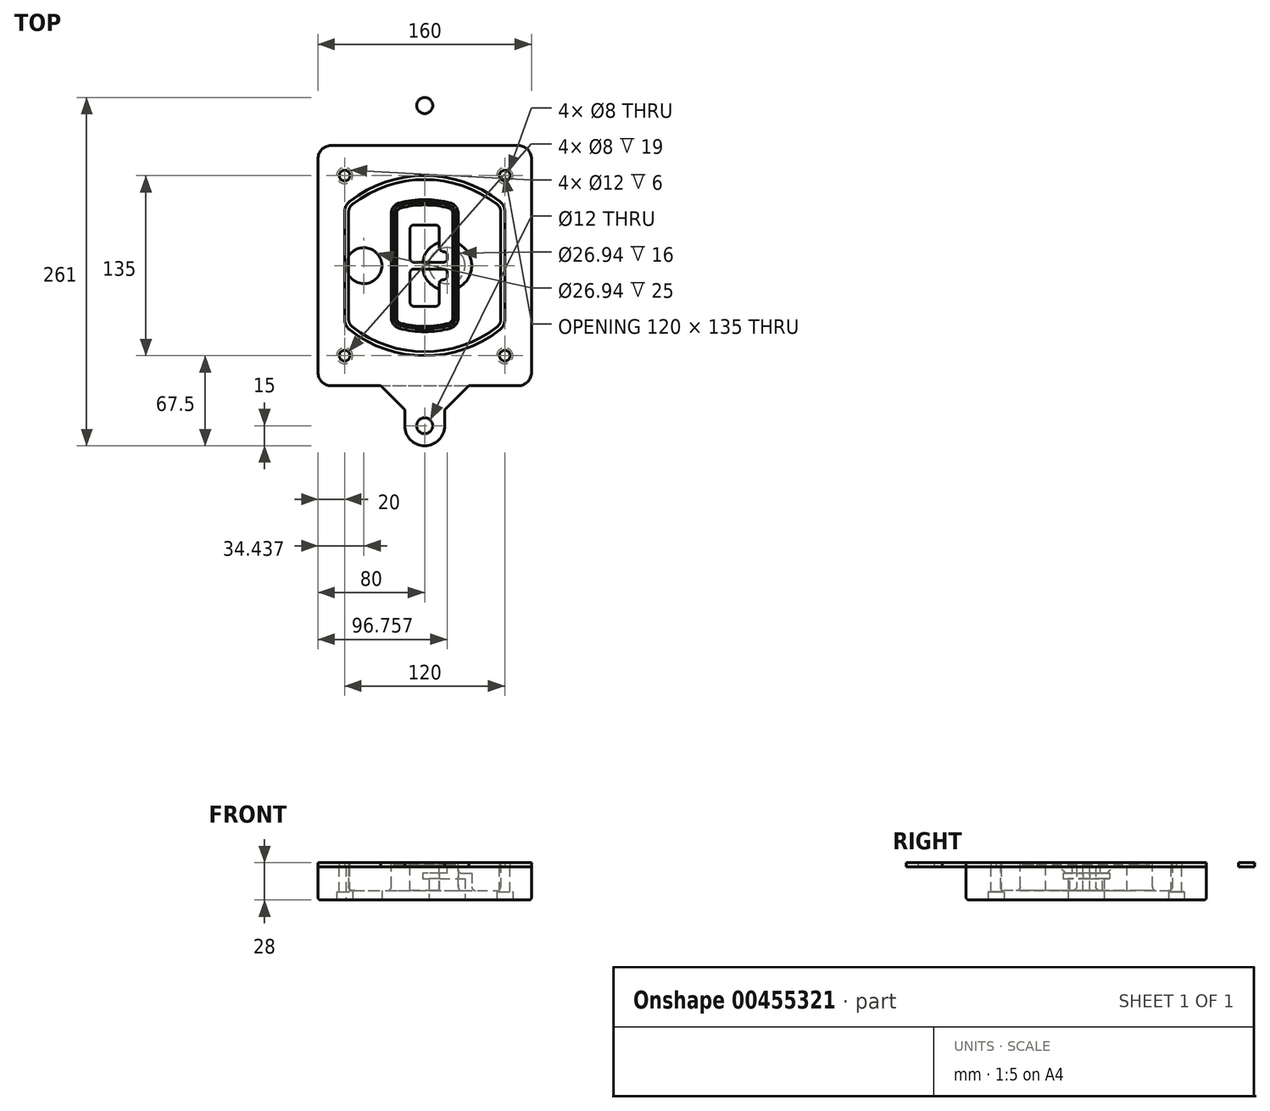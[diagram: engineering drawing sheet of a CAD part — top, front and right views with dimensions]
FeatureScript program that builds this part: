
annotation { "Feature Type Name" : "Feature", "Feature Type Description" : "" }
export const myFeature = defineFeature(function(context is Context, id is Id, definition is map)
    precondition{}
    {
        {
            var Q0;
            Q0=qCreatedBy(makeId("Top.planeOp"),FACE);
            var sketch = newSketch(context, id + "F0", { "sketchPlane" : qUnion([Q0])});
            skPoint(sketch, "E0.rect.middle", {"position": v(0, 0) * mm});
            skLineSegment(sketch, "E1.bottom", {"start": v(-70, -90) * mm, "end": v(70, -90) * mm});
            skLineSegment(sketch, "E1.top", {"start": v(-70, 90) * mm, "end": v(70, 90) * mm});
            skLineSegment(sketch, "E1.left", {"start": v(-80, -80) * mm, "end": v(-80, 80) * mm});
            skLineSegment(sketch, "E1.right", {"start": v(80, -80) * mm, "end": v(80, 80) * mm});
            skLineSegment(sketch, "E2", {"start": v(-80, 90) * mm, "end": v(80, -90) * mm, "construction": true});
            skLineSegment(sketch, "E3", {"start": v(80, 90) * mm, "end": v(-80, -90) * mm, "construction": true});
            skCircle(sketch, "E4", {"center": v(-60, 67.5) * mm, "radius": 4 * mm});
            skCircle(sketch, "E5", {"center": v(60, 67.5) * mm, "radius": 4 * mm});
            skCircle(sketch, "E6", {"center": v(60, -67.5) * mm, "radius": 4 * mm});
            skCircle(sketch, "E7", {"center": v(-60, -67.5) * mm, "radius": 4 * mm});
            skLineSegment(sketch, "E8", {"start": v(-60, 67.5) * mm, "end": v(60, 67.5) * mm, "construction": true});
            skLineSegment(sketch, "E9", {"start": v(60, 67.5) * mm, "end": v(60, -67.5) * mm, "construction": true});
            skLineSegment(sketch, "E10", {"start": v(60, -67.5) * mm, "end": v(-60, -67.5) * mm, "construction": true});
            skLineSegment(sketch, "E11", {"start": v(-60, -67.5) * mm, "end": v(-60, 67.5) * mm, "construction": true});
            skLineSegment(sketch, "E12", {"start": v(-60, 40.3) * mm, "end": v(-60, -40.3) * mm});
            skLineSegment(sketch, "E13", {"start": v(60, 40.3) * mm, "end": v(60, -40.3) * mm});
            skArc(sketch, "E14", {"start": v(56.15, 48.18) * mm, "mid": v(0, 67.5) * mm, "end": v(-56.15, 48.18) * mm});
            skArc(sketch, "E15", {"start": v(-56.15, -48.18) * mm, "mid": v(0, -67.5) * mm, "end": v(56.15, -48.18) * mm});
            skLineSegment(sketch, "E16", {"start": v(-60, 0) * mm, "end": v(60, 0) * mm, "construction": true});
            skPoint(sketch, "E17.visualSharp", {"position": v(-60, -45) * mm});
            skArc(sketch, "E17.filletArc", {"start": v(-60, -40.3) * mm, "mid": v(-58.99, -44.68) * mm, "end": v(-56.15, -48.18) * mm});
            skPoint(sketch, "E18.visualSharp", {"position": v(-60, 45) * mm});
            skArc(sketch, "E18.filletArc", {"start": v(-56.15, 48.18) * mm, "mid": v(-58.99, 44.68) * mm, "end": v(-60, 40.3) * mm});
            skPoint(sketch, "E19.visualSharp", {"position": v(60, 45) * mm});
            skArc(sketch, "E19.filletArc", {"start": v(60, 40.3) * mm, "mid": v(58.99, 44.68) * mm, "end": v(56.15, 48.18) * mm});
            skPoint(sketch, "E20.visualSharp", {"position": v(60, -45) * mm});
            skArc(sketch, "E20.filletArc", {"start": v(56.15, -48.18) * mm, "mid": v(58.99, -44.68) * mm, "end": v(60, -40.3) * mm});
            skPoint(sketch, "E21.visualSharp", {"position": v(-80, 90) * mm});
            skArc(sketch, "E21.filletArc", {"start": v(-70, 90) * mm, "mid": v(-77.07, 87.07) * mm, "end": v(-80, 80) * mm});
            skPoint(sketch, "E22.visualSharp", {"position": v(80, 90) * mm});
            skArc(sketch, "E22.filletArc", {"start": v(80, 80) * mm, "mid": v(77.07, 87.07) * mm, "end": v(70, 90) * mm});
            skPoint(sketch, "E23.visualSharp", {"position": v(80, -90) * mm});
            skArc(sketch, "E23.filletArc", {"start": v(70, -90) * mm, "mid": v(77.07, -87.07) * mm, "end": v(80, -80) * mm});
            skPoint(sketch, "E24.visualSharp", {"position": v(-80, -90) * mm});
            skArc(sketch, "E24.filletArc", {"start": v(-80, -80) * mm, "mid": v(-77.07, -87.07) * mm, "end": v(-70, -90) * mm});
            skArc(sketch, "E25.0", {"start": v(57, 40.3) * mm, "mid": v(56.3, 43.36) * mm, "end": v(54.3, 45.81) * mm});
            skLineSegment(sketch, "E25.1", {"start": v(57, 40.3) * mm, "end": v(57, -40.3) * mm});
            skArc(sketch, "E25.2", {"start": v(54.3, -45.81) * mm, "mid": v(56.3, -43.36) * mm, "end": v(57, -40.3) * mm});
            skArc(sketch, "E25.3", {"start": v(-54.3, -45.81) * mm, "mid": v(0, -64.5) * mm, "end": v(54.3, -45.81) * mm});
            skArc(sketch, "E25.4", {"start": v(-57, -40.3) * mm, "mid": v(-56.3, -43.36) * mm, "end": v(-54.3, -45.81) * mm});
            skArc(sketch, "E25.5", {"start": v(54.3, 45.81) * mm, "mid": v(0, 64.5) * mm, "end": v(-54.3, 45.81) * mm});
            skLineSegment(sketch, "E25.6", {"start": v(-57, 40.3) * mm, "end": v(-57, -40.3) * mm});
            skArc(sketch, "E25.7", {"start": v(-54.3, 45.81) * mm, "mid": v(-56.3, 43.36) * mm, "end": v(-57, 40.3) * mm});
            skArc(sketch, "E26.0", {"start": v(-58.62, 51.33) * mm, "mid": v(-62.58, 46.43) * mm, "end": v(-64, 40.3) * mm});
            skArc(sketch, "E26.1", {"start": v(58.62, 51.33) * mm, "mid": v(0, 71.5) * mm, "end": v(-58.62, 51.33) * mm});
            skArc(sketch, "E26.2", {"start": v(64, 40.3) * mm, "mid": v(62.58, 46.43) * mm, "end": v(58.62, 51.33) * mm});
            skLineSegment(sketch, "E26.3", {"start": v(64, 40.3) * mm, "end": v(64, -40.3) * mm});
            skArc(sketch, "E26.4", {"start": v(58.62, -51.33) * mm, "mid": v(62.58, -46.43) * mm, "end": v(64, -40.3) * mm});
            skLineSegment(sketch, "E26.5", {"start": v(-64, 40.3) * mm, "end": v(-64, -40.3) * mm});
            skArc(sketch, "E26.6", {"start": v(-58.62, -51.33) * mm, "mid": v(0, -71.5) * mm, "end": v(58.62, -51.33) * mm});
            skArc(sketch, "E26.7", {"start": v(-64, -40.3) * mm, "mid": v(-62.58, -46.43) * mm, "end": v(-58.62, -51.33) * mm});
            skSolve(sketch);
        }
        {
            var Q0;
            Q0=makeQuery(id+"F0.imprint","IMPRINT",FACE,{"disambiguationData":[TD([[makeQuery(id+"F0.imprint","IMPRINT",EDGE,{"derivedFrom":sQuery(id+"F0.wireOp",EDGE,"E1.bottom")}),1.0]])]});
            var Q1;
            Q1=makeQuery(id+"F0.imprint","IMPRINT",FACE,{"disambiguationData":[TD([[makeQuery(id+"F0.imprint","IMPRINT",EDGE,{"derivedFrom":sQuery(id+"F0.wireOp",EDGE,"E12")}),1.0]])]});
            var Q2;
            Q2=makeQuery(id+"F0.imprint","IMPRINT",FACE,{"disambiguationData":[TD([[makeQuery(id+"F0.imprint","IMPRINT",EDGE,{"derivedFrom":sQuery(id+"F0.wireOp",EDGE,"E25.0")}),1.0]])]});
            var Q3;
            Q3=makeQuery(id+"F0.imprint","IMPRINT",FACE,{"disambiguationData":[TD([[makeQuery(id+"F0.imprint","IMPRINT",EDGE,{"derivedFrom":sQuery(id+"F0.wireOp",EDGE,"E12")}),-1.0]])]});
            extrude(context, id + "F1", {"entities" : qUnion([Q0, Q1, Q2, Q3]), "oppositeDirection" : true, "depth" : 25 * mm});
        }
        {
            var Q0;
            Q0=makeQuery(id+"F0.imprint","IMPRINT",FACE,{"disambiguationData":[TD([[makeQuery(id+"F0.imprint","IMPRINT",EDGE,{"derivedFrom":sQuery(id+"F0.wireOp",EDGE,"E12")}),1.0]])]});
            extrude(context, id + "F2", {"entities" : qUnion([Q0]), "operationType" : NewBodyOperationType.ADD, "depth" : 3 * mm});
        }
        {
            var Q0;
            Q0=makeQuery(id+"F0.imprint","IMPRINT",FACE,{"disambiguationData":[TD([[makeQuery(id+"F0.imprint","IMPRINT",EDGE,{"derivedFrom":sQuery(id+"F0.wireOp",EDGE,"E25.0")}),1.0]])]});
            extrude(context, id + "F3", {"entities" : qUnion([Q0]), "operationType" : NewBodyOperationType.REMOVE, "oppositeDirection" : true, "depth" : 18 * mm});
        }
        {
            var Q0;
            Q0=makeQuery(id+"F2.opExtrude","CAP_FACE",FACE,{"disambiguationData":[OSD([sQuery(id+"F0.wireOp",EDGE,"E12"),sQuery(id+"F0.wireOp",EDGE,"E13"),sQuery(id+"F0.wireOp",EDGE,"E14"),sQuery(id+"F0.wireOp",EDGE,"E15"),sQuery(id+"F0.wireOp",EDGE,"E17.filletArc"),sQuery(id+"F0.wireOp",EDGE,"E18.filletArc"),sQuery(id+"F0.wireOp",EDGE,"E19.filletArc"),sQuery(id+"F0.wireOp",EDGE,"E20.filletArc"),sQuery(id+"F0.wireOp",EDGE,"E25.0"),sQuery(id+"F0.wireOp",EDGE,"E25.1"),sQuery(id+"F0.wireOp",EDGE,"E25.2"),sQuery(id+"F0.wireOp",EDGE,"E25.3"),sQuery(id+"F0.wireOp",EDGE,"E25.4"),sQuery(id+"F0.wireOp",EDGE,"E25.5"),sQuery(id+"F0.wireOp",EDGE,"E25.6"),sQuery(id+"F0.wireOp",EDGE,"E25.7")])],"isStart":false});
            var sketch = newSketch(context, id + "F4", { "sketchPlane" : qUnion([Q0])});
            skArc(sketch, "E27.0", {"start": v(-19.08, -46.97) * mm, "mid": v(0, -49.5) * mm, "end": v(19.08, -46.97) * mm});
            skArc(sketch, "E28.0", {"start": v(19.08, 46.97) * mm, "mid": v(0, 49.5) * mm, "end": v(-19.08, 46.97) * mm});
            skLineSegment(sketch, "E29", {"start": v(-25, 39.25) * mm, "end": v(-25, -39.25) * mm});
            skLineSegment(sketch, "E30", {"start": v(25, 39.25) * mm, "end": v(25, -39.25) * mm});
            skLineSegment(sketch, "E31", {"start": v(-25, 45.1) * mm, "end": v(25, 45.1) * mm, "construction": true});
            skLineSegment(sketch, "E32", {"start": v(-25, -45.1) * mm, "end": v(25, -45.1) * mm, "construction": true});
            skPoint(sketch, "E33.visualSharp", {"position": v(-25, 45.1) * mm});
            skArc(sketch, "E33.filletArc", {"start": v(-19.08, 46.97) * mm, "mid": v(-23.35, 44.11) * mm, "end": v(-25, 39.25) * mm});
            skPoint(sketch, "E34.visualSharp", {"position": v(25, 45.1) * mm});
            skArc(sketch, "E34.filletArc", {"start": v(25, 39.25) * mm, "mid": v(23.35, 44.11) * mm, "end": v(19.08, 46.97) * mm});
            skPoint(sketch, "E35.visualSharp", {"position": v(25, -45.1) * mm});
            skArc(sketch, "E35.filletArc", {"start": v(19.08, -46.97) * mm, "mid": v(23.35, -44.11) * mm, "end": v(25, -39.25) * mm});
            skPoint(sketch, "E36.visualSharp", {"position": v(-25, -45.1) * mm});
            skArc(sketch, "E36.filletArc", {"start": v(-25, -39.25) * mm, "mid": v(-23.35, -44.11) * mm, "end": v(-19.08, -46.97) * mm});
            skArc(sketch, "E37.0", {"start": v(54.3, 45.81) * mm, "mid": v(0, 64.5) * mm, "end": v(-54.3, 45.81) * mm});
            skArc(sketch, "E37.1", {"start": v(-54.3, 45.81) * mm, "mid": v(-56.3, 43.36) * mm, "end": v(-57, 40.3) * mm});
            skLineSegment(sketch, "E37.2", {"start": v(-57, 40.3) * mm, "end": v(-57, -40.3) * mm});
            skArc(sketch, "E37.3", {"start": v(-57, -40.3) * mm, "mid": v(-56.3, -43.36) * mm, "end": v(-54.3, -45.81) * mm});
            skArc(sketch, "E37.4", {"start": v(-54.3, -45.81) * mm, "mid": v(0, -64.5) * mm, "end": v(54.3, -45.81) * mm});
            skArc(sketch, "E37.5", {"start": v(54.3, -45.81) * mm, "mid": v(56.3, -43.36) * mm, "end": v(57, -40.3) * mm});
            skLineSegment(sketch, "E37.6", {"start": v(57, 40.3) * mm, "end": v(57, -40.3) * mm});
            skArc(sketch, "E37.7", {"start": v(57, 40.3) * mm, "mid": v(56.3, 43.36) * mm, "end": v(54.3, 45.81) * mm});
            skLineSegment(sketch, "E38.0", {"start": v(23, 39.25) * mm, "end": v(23, -39.25) * mm});
            skArc(sketch, "E38.1", {"start": v(18.56, -45.04) * mm, "mid": v(21.76, -42.9) * mm, "end": v(23, -39.25) * mm});
            skArc(sketch, "E38.2", {"start": v(-18.56, -45.04) * mm, "mid": v(0, -47.5) * mm, "end": v(18.56, -45.04) * mm});
            skArc(sketch, "E38.3", {"start": v(-23, -39.25) * mm, "mid": v(-21.76, -42.9) * mm, "end": v(-18.56, -45.04) * mm});
            skLineSegment(sketch, "E38.4", {"start": v(-23, 39.25) * mm, "end": v(-23, -39.25) * mm});
            skArc(sketch, "E38.5", {"start": v(23, 39.25) * mm, "mid": v(21.76, 42.9) * mm, "end": v(18.56, 45.04) * mm});
            skArc(sketch, "E38.6", {"start": v(-18.56, 45.04) * mm, "mid": v(-21.76, 42.9) * mm, "end": v(-23, 39.25) * mm});
            skArc(sketch, "E38.7", {"start": v(18.56, 45.04) * mm, "mid": v(0, 47.5) * mm, "end": v(-18.56, 45.04) * mm});
            skArc(sketch, "E39.0", {"start": v(21, 39.25) * mm, "mid": v(20.18, 41.68) * mm, "end": v(18.04, 43.1) * mm});
            skLineSegment(sketch, "E39.1", {"start": v(21, 39.25) * mm, "end": v(21, -39.25) * mm});
            skArc(sketch, "E39.2", {"start": v(18.04, -43.1) * mm, "mid": v(20.18, -41.68) * mm, "end": v(21, -39.25) * mm});
            skArc(sketch, "E39.3", {"start": v(-18.04, -43.1) * mm, "mid": v(0, -45.5) * mm, "end": v(18.04, -43.1) * mm});
            skArc(sketch, "E39.4", {"start": v(-21, -39.25) * mm, "mid": v(-20.18, -41.68) * mm, "end": v(-18.04, -43.1) * mm});
            skArc(sketch, "E39.5", {"start": v(18.04, 43.1) * mm, "mid": v(0, 45.5) * mm, "end": v(-18.04, 43.1) * mm});
            skLineSegment(sketch, "E39.6", {"start": v(-21, 39.25) * mm, "end": v(-21, -39.25) * mm});
            skArc(sketch, "E39.7", {"start": v(-18.04, 43.1) * mm, "mid": v(-20.18, 41.68) * mm, "end": v(-21, 39.25) * mm});
            skLineSegment(sketch, "E40", {"start": v(-25, 0) * mm, "end": v(25, 0) * mm, "construction": true});
            skLineSegment(sketch, "E41", {"start": v(-11, 5.5) * mm, "end": v(-11, 27.5) * mm});
            skLineSegment(sketch, "E42", {"start": v(-8, 30.5) * mm, "end": v(8, 30.5) * mm});
            skLineSegment(sketch, "E43", {"start": v(11, 27.5) * mm, "end": v(11, 13.5) * mm});
            skLineSegment(sketch, "E44", {"start": v(14, 10.5) * mm, "end": v(14, 10.5) * mm});
            skLineSegment(sketch, "E45", {"start": v(17, 7.5) * mm, "end": v(17, 5.5) * mm});
            skLineSegment(sketch, "E46", {"start": v(14, 2.5) * mm, "end": v(-8, 2.5) * mm});
            skPoint(sketch, "E47.visualSharp", {"position": v(-11, 30.5) * mm});
            skArc(sketch, "E47.filletArc", {"start": v(-8, 30.5) * mm, "mid": v(-10.12, 29.62) * mm, "end": v(-11, 27.5) * mm});
            skPoint(sketch, "E48.visualSharp", {"position": v(11, 30.5) * mm});
            skArc(sketch, "E48.filletArc", {"start": v(11, 27.5) * mm, "mid": v(10.12, 29.62) * mm, "end": v(8, 30.5) * mm});
            skPoint(sketch, "E49.visualSharp", {"position": v(11, 10.5) * mm});
            skArc(sketch, "E49.filletArc", {"start": v(11, 13.5) * mm, "mid": v(11.88, 11.38) * mm, "end": v(14, 10.5) * mm});
            skPoint(sketch, "E50.visualSharp", {"position": v(17, 10.5) * mm});
            skArc(sketch, "E50.filletArc", {"start": v(17, 7.5) * mm, "mid": v(16.12, 9.62) * mm, "end": v(14, 10.5) * mm});
            skPoint(sketch, "E51.visualSharp", {"position": v(17, 2.5) * mm});
            skArc(sketch, "E51.filletArc", {"start": v(14, 2.5) * mm, "mid": v(16.12, 3.38) * mm, "end": v(17, 5.5) * mm});
            skPoint(sketch, "E52.visualSharp", {"position": v(-11, 2.5) * mm});
            skArc(sketch, "E52.filletArc", {"start": v(-11, 5.5) * mm, "mid": v(-10.12, 3.38) * mm, "end": v(-8, 2.5) * mm});
            skLineSegment(sketch, "E53.0.MirrorCS", {"start": v(14, -2.5) * mm, "end": v(-8, -2.5) * mm});
            skArc(sketch, "E54.0.MirrorCS", {"start": v(-11, -5.5) * mm, "mid": v(-10.12, -3.38) * mm, "end": v(-8, -2.5) * mm});
            skLineSegment(sketch, "E55.0.MirrorCS", {"start": v(-11, -5.5) * mm, "end": v(-11, -27.5) * mm});
            skArc(sketch, "E56.0.MirrorCS", {"start": v(-8, -30.5) * mm, "mid": v(-10.12, -29.62) * mm, "end": v(-11, -27.5) * mm});
            skLineSegment(sketch, "E57.0.MirrorCS", {"start": v(-8, -30.5) * mm, "end": v(8, -30.5) * mm});
            skArc(sketch, "E58.0.MirrorCS", {"start": v(11, -27.5) * mm, "mid": v(10.12, -29.62) * mm, "end": v(8, -30.5) * mm});
            skLineSegment(sketch, "E59.0.MirrorCS", {"start": v(11, -27.5) * mm, "end": v(11, -13.5) * mm});
            skArc(sketch, "E60.0.MirrorCS", {"start": v(11, -13.5) * mm, "mid": v(11.88, -11.38) * mm, "end": v(14, -10.5) * mm});
            skArc(sketch, "E61.0.MirrorCS", {"start": v(17, -7.5) * mm, "mid": v(16.12, -9.62) * mm, "end": v(14, -10.5) * mm});
            skLineSegment(sketch, "E62.0.MirrorCS", {"start": v(17, -7.5) * mm, "end": v(17, -5.5) * mm});
            skArc(sketch, "E63.0.MirrorCS", {"start": v(14, -2.5) * mm, "mid": v(16.12, -3.38) * mm, "end": v(17, -5.5) * mm});
            skSolve(sketch);
        }
        {
            var Q0;
            Q0=makeQuery(id+"F4.imprint","IMPRINT",FACE,{"disambiguationData":[TD([[makeQuery(id+"F4.imprint","IMPRINT",EDGE,{"derivedFrom":sQuery(id+"F4.wireOp",EDGE,"E27.0")}),1.0]])]});
            var Q1;
            Q1=makeQuery(id+"F4.imprint","IMPRINT",FACE,{"disambiguationData":[TD([[makeQuery(id+"F4.imprint","IMPRINT",EDGE,{"derivedFrom":sQuery(id+"F4.wireOp",EDGE,"E38.0")}),-1.0]])]});
            var Q2;
            Q2=makeQuery(id+"F4.imprint","IMPRINT",FACE,{"disambiguationData":[TD([[makeQuery(id+"F4.imprint","IMPRINT",EDGE,{"derivedFrom":sQuery(id+"F4.wireOp",EDGE,"E39.0")}),1.0]])]});
            extrude(context, id + "F5", {"entities" : qUnion([Q0, Q1, Q2]), "operationType" : NewBodyOperationType.ADD, "endBound" : BoundingType.UP_TO_NEXT, "oppositeDirection" : true, "depth" : 25 * mm});
        }
        {
            var Q0;
            Q0=makeQuery(id+"F4.imprint","IMPRINT",FACE,{"disambiguationData":[TD([[makeQuery(id+"F4.imprint","IMPRINT",EDGE,{"derivedFrom":sQuery(id+"F4.wireOp",EDGE,"E38.0")}),-1.0]])]});
            extrude(context, id + "F6", {"entities" : qUnion([Q0]), "operationType" : NewBodyOperationType.REMOVE, "oppositeDirection" : true, "depth" : 2 * mm});
        }
        {
            var Q0;
            Q0=makeQuery(id+"F1.opExtrude","CAP_FACE",FACE,{"disambiguationData":[OSD([sQuery(id+"F0.wireOp",EDGE,"E1.bottom"),sQuery(id+"F0.wireOp",EDGE,"E1.top"),sQuery(id+"F0.wireOp",EDGE,"E1.left"),sQuery(id+"F0.wireOp",EDGE,"E1.right"),sQuery(id+"F0.wireOp",EDGE,"E4"),sQuery(id+"F0.wireOp",EDGE,"E5"),sQuery(id+"F0.wireOp",EDGE,"E6"),sQuery(id+"F0.wireOp",EDGE,"E7"),sQuery(id+"F0.wireOp",EDGE,"E21.filletArc"),sQuery(id+"F0.wireOp",EDGE,"E22.filletArc"),sQuery(id+"F0.wireOp",EDGE,"E23.filletArc"),sQuery(id+"F0.wireOp",EDGE,"E24.filletArc")])],"isStart":false});
            var sketch = newSketch(context, id + "F7", { "sketchPlane" : qUnion([Q0])});
            skCircle(sketch, "E64", {"center": v(16.76, 0) * mm, "radius": 13.47 * mm});
            skCircle(sketch, "E65", {"center": v(-45.56, 0) * mm, "radius": 13.47 * mm});
            skLineSegment(sketch, "E66", {"start": v(80, 0) * mm, "end": v(-80, 0) * mm});
            skCircle(sketch, "E67", {"center": v(16.76, 0) * mm, "radius": 18.47 * mm});
            skCircle(sketch, "E68", {"center": v(60, -67.5) * mm, "radius": 6 * mm});
            skCircle(sketch, "E69", {"center": v(-60, -67.5) * mm, "radius": 6 * mm});
            skCircle(sketch, "E70", {"center": v(-60, 67.5) * mm, "radius": 6 * mm});
            skCircle(sketch, "E71", {"center": v(60, 67.5) * mm, "radius": 6 * mm});
            skSolve(sketch);
        }
        {
            var Q0;
            {var subQ1=sQuery(id+"F7.wireOp",EDGE,"E66");var subQ4=sQuery(id+"F7.wireOp",EDGE,"E64");var subQ6=makeQuery(id+"F7.imprint","INTERSECT",VERTEX,{"disambiguationData":[OD(0.0)],"derivedFrom":[subQ4,subQ1]});Q0=makeQuery(id+"F7.imprint","IMPRINT",FACE,{"disambiguationData":[TD([[makeQuery(id+"F7.imprint","IMPRINT",EDGE,{"disambiguationData":[TD([[subQ6,-1.0]])],"derivedFrom":subQ4}),-1.0]])]});}
            var Q1;
            {var subQ0=sQuery(id+"F7.wireOp",EDGE,"E66");var subQ1=sQuery(id+"F7.wireOp",EDGE,"E64");var subQ3=makeQuery(id+"F7.imprint","INTERSECT",VERTEX,{"disambiguationData":[OD(0.0)],"derivedFrom":[subQ1,subQ0]});Q1=makeQuery(id+"F7.imprint","IMPRINT",FACE,{"disambiguationData":[TD([[makeQuery(id+"F7.imprint","IMPRINT",EDGE,{"disambiguationData":[TD([[subQ3,-1.0]])],"derivedFrom":subQ1}),1.0]])]});}
            var Q2;
            {var subQ0=sQuery(id+"F7.wireOp",EDGE,"E66");var subQ1=sQuery(id+"F7.wireOp",EDGE,"E64");var subQ3=makeQuery(id+"F7.imprint","INTERSECT",VERTEX,{"disambiguationData":[OD(0.0)],"derivedFrom":[subQ1,subQ0]});Q2=makeQuery(id+"F7.imprint","IMPRINT",FACE,{"disambiguationData":[TD([[makeQuery(id+"F7.imprint","IMPRINT",EDGE,{"disambiguationData":[TD([[subQ3,1.0]])],"derivedFrom":subQ1}),1.0]])]});}
            var Q3;
            {var subQ1=sQuery(id+"F7.wireOp",EDGE,"E66");var subQ4=sQuery(id+"F7.wireOp",EDGE,"E64");var subQ6=makeQuery(id+"F7.imprint","INTERSECT",VERTEX,{"disambiguationData":[OD(0.0)],"derivedFrom":[subQ4,subQ1]});Q3=makeQuery(id+"F7.imprint","IMPRINT",FACE,{"disambiguationData":[TD([[makeQuery(id+"F7.imprint","IMPRINT",EDGE,{"disambiguationData":[TD([[subQ6,1.0]])],"derivedFrom":subQ4}),-1.0]])]});}
            extrude(context, id + "F8", {"entities" : qUnion([Q0, Q1, Q2, Q3]), "operationType" : NewBodyOperationType.ADD, "oppositeDirection" : true, "depth" : 20 * mm});
        }
        {
            var Q0;
            {var subQ0=sQuery(id+"F7.wireOp",EDGE,"E66");var subQ1=sQuery(id+"F7.wireOp",EDGE,"E64");var subQ3=makeQuery(id+"F7.imprint","INTERSECT",VERTEX,{"disambiguationData":[OD(0.0)],"derivedFrom":[subQ1,subQ0]});Q0=makeQuery(id+"F7.imprint","IMPRINT",FACE,{"disambiguationData":[TD([[makeQuery(id+"F7.imprint","IMPRINT",EDGE,{"disambiguationData":[TD([[subQ3,-1.0]])],"derivedFrom":subQ1}),1.0]])]});}
            var Q1;
            {var subQ0=sQuery(id+"F7.wireOp",EDGE,"E66");var subQ1=sQuery(id+"F7.wireOp",EDGE,"E64");var subQ3=makeQuery(id+"F7.imprint","INTERSECT",VERTEX,{"disambiguationData":[OD(0.0)],"derivedFrom":[subQ1,subQ0]});Q1=makeQuery(id+"F7.imprint","IMPRINT",FACE,{"disambiguationData":[TD([[makeQuery(id+"F7.imprint","IMPRINT",EDGE,{"disambiguationData":[TD([[subQ3,1.0]])],"derivedFrom":subQ1}),1.0]])]});}
            extrude(context, id + "F9", {"entities" : qUnion([Q0, Q1]), "operationType" : NewBodyOperationType.REMOVE, "oppositeDirection" : true, "depth" : 16 * mm});
        }
        {
            var Q0;
            {var subQ0=sQuery(id+"F7.wireOp",EDGE,"E66");var subQ1=sQuery(id+"F7.wireOp",EDGE,"E65");var subQ3=makeQuery(id+"F7.imprint","INTERSECT",VERTEX,{"disambiguationData":[OD(0.0)],"derivedFrom":[subQ1,subQ0]});Q0=makeQuery(id+"F7.imprint","IMPRINT",FACE,{"disambiguationData":[TD([[makeQuery(id+"F7.imprint","IMPRINT",EDGE,{"disambiguationData":[TD([[subQ3,-1.0]])],"derivedFrom":subQ1}),1.0]])]});}
            var Q1;
            {var subQ0=sQuery(id+"F7.wireOp",EDGE,"E66");var subQ1=sQuery(id+"F7.wireOp",EDGE,"E65");var subQ3=makeQuery(id+"F7.imprint","INTERSECT",VERTEX,{"disambiguationData":[OD(0.0)],"derivedFrom":[subQ1,subQ0]});Q1=makeQuery(id+"F7.imprint","IMPRINT",FACE,{"disambiguationData":[TD([[makeQuery(id+"F7.imprint","IMPRINT",EDGE,{"disambiguationData":[TD([[subQ3,1.0]])],"derivedFrom":subQ1}),1.0]])]});}
            extrude(context, id + "F10", {"entities" : qUnion([Q0, Q1]), "operationType" : NewBodyOperationType.REMOVE, "oppositeDirection" : true, "depth" : 25 * mm});
        }
        {
            var Q0;
            Q0=makeQuery(id+"F7.imprint","IMPRINT",FACE,{"disambiguationData":[TD([[makeQuery(id+"F7.imprint","IMPRINT",EDGE,{"derivedFrom":sQuery(id+"F7.wireOp",EDGE,"E68")}),1.0]])]});
            var Q1;
            Q1=makeQuery(id+"F7.imprint","IMPRINT",FACE,{"disambiguationData":[TD([[makeQuery(id+"F7.imprint","IMPRINT",EDGE,{"derivedFrom":makeQuery(id+"F1.opExtrude","CAP_EDGE",EDGE,{"disambiguationData":[OSD([sQuery(id+"F0.wireOp",EDGE,"E5")])],"isStart":false})}),-1.0]])]});
            var Q2;
            Q2=makeQuery(id+"F7.imprint","IMPRINT",FACE,{"disambiguationData":[TD([[makeQuery(id+"F7.imprint","IMPRINT",EDGE,{"derivedFrom":sQuery(id+"F7.wireOp",EDGE,"E69")}),1.0]])]});
            var Q3;
            Q3=makeQuery(id+"F7.imprint","IMPRINT",FACE,{"disambiguationData":[TD([[makeQuery(id+"F7.imprint","IMPRINT",EDGE,{"derivedFrom":makeQuery(id+"F1.opExtrude","CAP_EDGE",EDGE,{"disambiguationData":[OSD([sQuery(id+"F0.wireOp",EDGE,"E4")])],"isStart":false})}),-1.0]])]});
            var Q4;
            Q4=makeQuery(id+"F7.imprint","IMPRINT",FACE,{"disambiguationData":[TD([[makeQuery(id+"F7.imprint","IMPRINT",EDGE,{"derivedFrom":sQuery(id+"F7.wireOp",EDGE,"E70")}),1.0]])]});
            var Q5;
            Q5=makeQuery(id+"F7.imprint","IMPRINT",FACE,{"disambiguationData":[TD([[makeQuery(id+"F7.imprint","IMPRINT",EDGE,{"derivedFrom":makeQuery(id+"F1.opExtrude","CAP_EDGE",EDGE,{"disambiguationData":[OSD([sQuery(id+"F0.wireOp",EDGE,"E7")])],"isStart":false})}),-1.0]])]});
            var Q6;
            Q6=makeQuery(id+"F7.imprint","IMPRINT",FACE,{"disambiguationData":[TD([[makeQuery(id+"F7.imprint","IMPRINT",EDGE,{"derivedFrom":sQuery(id+"F7.wireOp",EDGE,"E71")}),1.0]])]});
            var Q7;
            Q7=makeQuery(id+"F7.imprint","IMPRINT",FACE,{"disambiguationData":[TD([[makeQuery(id+"F7.imprint","IMPRINT",EDGE,{"derivedFrom":makeQuery(id+"F1.opExtrude","CAP_EDGE",EDGE,{"disambiguationData":[OSD([sQuery(id+"F0.wireOp",EDGE,"E6")])],"isStart":false})}),-1.0]])]});
            extrude(context, id + "F11", {"entities" : qUnion([Q0, Q1, Q2, Q3, Q4, Q5, Q6, Q7]), "operationType" : NewBodyOperationType.REMOVE, "oppositeDirection" : true, "depth" : 6 * mm});
        }
        {
            var Q0;
            Q0=makeQuery(id+"F9.boolean.opBoolean","COPY",FACE,{"derivedFrom":makeQuery(id+"F9.opExtrude","CAP_FACE",FACE,{"disambiguationData":[OSD([sQuery(id+"F7.wireOp",EDGE,"E64")])],"isStart":false})});
            var sketch = newSketch(context, id + "F12", { "sketchPlane" : qUnion([Q0])});
            skArc(sketch, "E72.0", {"start": v(11, 17.55) * mm, "mid": v(2.57, 11.82) * mm, "end": v(-1.54, 2.5) * mm});
            skArc(sketch, "E72.1", {"start": v(-1.54, -2.5) * mm, "mid": v(2.57, -11.82) * mm, "end": v(11, -17.55) * mm});
            skLineSegment(sketch, "E73", {"start": v(-1.54, -2.5) * mm, "end": v(14, -2.5) * mm});
            skLineSegment(sketch, "E74.0", {"start": v(14, 2.5) * mm, "end": v(-1.54, 2.5) * mm});
            skArc(sketch, "E74.1", {"start": v(14, 2.5) * mm, "mid": v(16.12, 3.38) * mm, "end": v(17, 5.5) * mm});
            skLineSegment(sketch, "E74.2", {"start": v(17, 7.5) * mm, "end": v(17, 5.5) * mm});
            skArc(sketch, "E74.3", {"start": v(17, 7.5) * mm, "mid": v(16.12, 9.62) * mm, "end": v(14, 10.5) * mm});
            skArc(sketch, "E74.4", {"start": v(11, 13.5) * mm, "mid": v(11.88, 11.38) * mm, "end": v(14, 10.5) * mm});
            skLineSegment(sketch, "E74.5", {"start": v(11, 17.55) * mm, "end": v(11, 13.5) * mm});
            skLineSegment(sketch, "E74.7", {"start": v(14, -2.5) * mm, "end": v(-1.54, -2.5) * mm});
            skArc(sketch, "E74.8", {"start": v(14, -2.5) * mm, "mid": v(16.12, -3.38) * mm, "end": v(17, -5.5) * mm});
            skLineSegment(sketch, "E74.9", {"start": v(17, -7.5) * mm, "end": v(17, -5.5) * mm});
            skArc(sketch, "E74.10", {"start": v(17, -7.5) * mm, "mid": v(16.12, -9.62) * mm, "end": v(14, -10.5) * mm});
            skArc(sketch, "E74.11", {"start": v(11, -13.5) * mm, "mid": v(11.88, -11.38) * mm, "end": v(14, -10.5) * mm});
            skLineSegment(sketch, "E74.12", {"start": v(11, -17.55) * mm, "end": v(11, -13.5) * mm});
            skPoint(sketch, "E75.orphan", {"position": v(11, -27.5) * mm});
            skPoint(sketch, "E76.orphan", {"position": v(-8, -2.5) * mm});
            skPoint(sketch, "E77.orphan", {"position": v(-8, 2.5) * mm});
            skPoint(sketch, "E78.orphan", {"position": v(11, 27.5) * mm});
            skSolve(sketch);
        }
        {
            var Q0;
            {var subQ7=sQuery(id+"F12.wireOp",EDGE,"E72.0");var subQ14=sQuery(id+"F12.wireOp",EDGE,"E72.1");var subQ16=sQuery(id+"F12.wireOp",EDGE,"E74.1");var subQ18=sQuery(id+"F12.wireOp",EDGE,"E74.8");Q0=qUnion([makeQuery(id+"F12.imprint","IMPRINT",FACE,{"disambiguationData":[TD([[makeQuery(id+"F12.imprint","IMPRINT",EDGE,{"derivedFrom":subQ7}),1.0]])]}),makeQuery(id+"F12.imprint","IMPRINT",FACE,{"disambiguationData":[TD([[makeQuery(id+"F12.imprint","IMPRINT",EDGE,{"derivedFrom":subQ14}),1.0]])]}),makeQuery(id+"F12.imprint","IMPRINT",FACE,{"disambiguationData":[TD([[makeQuery(id+"F12.imprint","IMPRINT",EDGE,{"derivedFrom":subQ16}),1.0]])]}),makeQuery(id+"F12.imprint","IMPRINT",FACE,{"disambiguationData":[TD([[makeQuery(id+"F12.imprint","IMPRINT",EDGE,{"derivedFrom":subQ18}),-1.0]])]})]);}
            var Q1;
            Q1=makeQuery(id+"F5.boolean.opBoolean","SPLIT",FACE,{"disambiguationData":[TD([makeQuery(id+"F5.opExtrude","SWEPT_FACE",FACE,{"disambiguationData":[OSD([sQuery(id+"F4.wireOp",EDGE,"E41")])]})])],"derivedFrom":makeQuery(id+"F3.boolean.opBoolean","COPY",FACE,{"derivedFrom":makeQuery(id+"F3.opExtrude","CAP_FACE",FACE,{"disambiguationData":[OSD([sQuery(id+"F0.wireOp",EDGE,"E25.0"),sQuery(id+"F0.wireOp",EDGE,"E25.1"),sQuery(id+"F0.wireOp",EDGE,"E25.2"),sQuery(id+"F0.wireOp",EDGE,"E25.3"),sQuery(id+"F0.wireOp",EDGE,"E25.4"),sQuery(id+"F0.wireOp",EDGE,"E25.5"),sQuery(id+"F0.wireOp",EDGE,"E25.6"),sQuery(id+"F0.wireOp",EDGE,"E25.7")])],"isStart":false})})});
            extrude(context, id + "F13", {"entities" : qUnion([Q0]), "operationType" : NewBodyOperationType.REMOVE, "endBound" : BoundingType.UP_TO_SURFACE, "endBoundEntityFace" : qUnion([Q1]), "depth" : 25 * mm});
        }
        {
            var Q0;
            Q0=makeQuery(id+"F3.boolean.opBoolean","COPY",EDGE,{"derivedFrom":makeQuery(id+"F3.opExtrude","CAP_EDGE",EDGE,{"disambiguationData":[OSD([sQuery(id+"F0.wireOp",EDGE,"E25.6")])],"isStart":false})});
            var Q1;
            Q1=makeQuery(id+"F8.boolean.opBoolean","INTERSECT",EDGE,{"derivedFrom":[makeQuery(id+"F5.opExtrude","SWEPT_FACE",FACE,{"disambiguationData":[OSD([sQuery(id+"F4.wireOp",EDGE,"E30")])]}),makeQuery(id+"F8.opExtrude","CAP_FACE",FACE,{"disambiguationData":[OSD([sQuery(id+"F7.wireOp",EDGE,"E67")])],"isStart":false})]});
            var Q2;
            Q2=makeQuery(id+"F8.boolean.opBoolean","INTERSECT",EDGE,{"disambiguationData":[OD(1.0)],"derivedFrom":[makeQuery(id+"F5.opExtrude","SWEPT_FACE",FACE,{"disambiguationData":[OSD([sQuery(id+"F4.wireOp",EDGE,"E30")])]}),makeQuery(id+"F8.opExtrude","SWEPT_FACE",FACE,{"disambiguationData":[OSD([sQuery(id+"F7.wireOp",EDGE,"E67")])]})]});
            var Q3;
            {var subQ0=sQuery(id+"F4.wireOp",EDGE,"E30");Q3=makeQuery(id+"F8.boolean.opBoolean","SPLIT",EDGE,{"disambiguationData":[TD([makeQuery(id+"F5.opExtrude","SWEPT_FACE",FACE,{"disambiguationData":[OSD([sQuery(id+"F4.wireOp",EDGE,"E35.filletArc")])]})])],"derivedFrom":makeQuery(id+"F5.opExtrude","CAP_EDGE",EDGE,{"disambiguationData":[OSD([subQ0])],"isStart":false})});}
            var Q4;
            {var subQ0=sQuery(id+"F0.wireOp",EDGE,"E25.7");var subQ1=sQuery(id+"F0.wireOp",EDGE,"E25.1");var subQ2=sQuery(id+"F0.wireOp",EDGE,"E25.6");var subQ3=sQuery(id+"F0.wireOp",EDGE,"E25.5");var subQ4=sQuery(id+"F0.wireOp",EDGE,"E25.4");var subQ5=sQuery(id+"F0.wireOp",EDGE,"E25.0");var subQ6=sQuery(id+"F0.wireOp",EDGE,"E25.2");var subQ7=sQuery(id+"F0.wireOp",EDGE,"E25.3");Q4=makeQuery(id+"F8.boolean.opBoolean","INTERSECT",EDGE,{"derivedFrom":[makeQuery(id+"F5.boolean.opBoolean","SPLIT",FACE,{"disambiguationData":[TD([makeQuery(id+"F2.opExtrude","SWEPT_FACE",FACE,{"disambiguationData":[OSD([subQ5])]})])],"derivedFrom":makeQuery(id+"F3.boolean.opBoolean","COPY",FACE,{"derivedFrom":makeQuery(id+"F3.opExtrude","CAP_FACE",FACE,{"disambiguationData":[OSD([subQ5,subQ1,subQ6,subQ7,subQ4,subQ3,subQ2,subQ0])],"isStart":false})})}),makeQuery(id+"F8.opExtrude","SWEPT_FACE",FACE,{"disambiguationData":[OSD([sQuery(id+"F7.wireOp",EDGE,"E67")])]})]});}
            var Q5;
            Q5=makeQuery(id+"F8.boolean.opBoolean","INTERSECT",EDGE,{"disambiguationData":[OD(0.0)],"derivedFrom":[makeQuery(id+"F5.opExtrude","SWEPT_FACE",FACE,{"disambiguationData":[OSD([sQuery(id+"F4.wireOp",EDGE,"E30")])]}),makeQuery(id+"F8.opExtrude","SWEPT_FACE",FACE,{"disambiguationData":[OSD([sQuery(id+"F7.wireOp",EDGE,"E67")])]})]});
            fillet(context, id + "F14", {"entities" : qUnion([Q0, Q1, Q2, Q3, Q4, Q5]), "radius" : 3 * mm, "tangentPropagation" : true, "allowEdgeOverflow" : false});
        }
        {
            var Q0;
            Q0=makeQuery(id+"F1.opExtrude","CAP_EDGE",EDGE,{"disambiguationData":[OSD([sQuery(id+"F0.wireOp",EDGE,"E1.bottom")])],"isStart":false});
            fillet(context, id + "F15", {"entities" : qUnion([Q0]), "radius" : 2 * mm, "tangentPropagation" : true, "allowEdgeOverflow" : false});
        }
        {
            var Q0;
            {var subQ0=sQuery(id+"F0.wireOp",EDGE,"E21.filletArc");var subQ1=sQuery(id+"F0.wireOp",EDGE,"E7");var subQ2=sQuery(id+"F0.wireOp",EDGE,"E6");var subQ3=sQuery(id+"F0.wireOp",EDGE,"E5");var subQ4=sQuery(id+"F0.wireOp",EDGE,"E4");var subQ5=sQuery(id+"F0.wireOp",EDGE,"E22.filletArc");var subQ6=sQuery(id+"F0.wireOp",EDGE,"E1.bottom");var subQ7=sQuery(id+"F0.wireOp",EDGE,"E1.right");var subQ8=sQuery(id+"F0.wireOp",EDGE,"E1.top");var subQ9=sQuery(id+"F0.wireOp",EDGE,"E1.left");var subQ10=sQuery(id+"F0.wireOp",EDGE,"E23.filletArc");var subQ11=sQuery(id+"F0.wireOp",EDGE,"E24.filletArc");Q0=makeQuery(id+"F2.boolean.opBoolean","SPLIT",FACE,{"disambiguationData":[TD([makeQuery(id+"F1.opExtrude","SWEPT_FACE",FACE,{"disambiguationData":[OSD([subQ6])]})])],"derivedFrom":makeQuery(id+"F1.opExtrude","CAP_FACE",FACE,{"disambiguationData":[OSD([subQ6,subQ8,subQ9,subQ7,subQ4,subQ3,subQ2,subQ1,subQ0,subQ5,subQ10,subQ11])],"isStart":true})});}
            var sketch = newSketch(context, id + "F16", { "sketchPlane" : qUnion([Q0])});
            skCircle(sketch, "E79", {"center": v(0, 120) * mm, "radius": 6 * mm});
            skPoint(sketch, "E79.centerSnap0", {"position": v(0, 90) * mm});
            skLineSegment(sketch, "E80", {"start": v(-33, 90) * mm, "end": v(-15, 108) * mm});
            skLineSegment(sketch, "E81", {"start": v(33, 90) * mm, "end": v(15, 108) * mm});
            skLineSegment(sketch, "E82", {"start": v(-15, 108) * mm, "end": v(-15, 120) * mm});
            skLineSegment(sketch, "E83", {"start": v(15, 108) * mm, "end": v(15, 120) * mm});
            skArc(sketch, "E84", {"start": v(15, 120) * mm, "mid": v(0, 135) * mm, "end": v(-15, 120) * mm});
            skLineSegment(sketch, "E85", {"start": v(0, 90) * mm, "end": v(0, 120) * mm, "construction": true});
            skLineSegment(sketch, "E86", {"start": v(-80, 0) * mm, "end": v(80, 0) * mm, "construction": true});
            skArc(sketch, "E87.MirrorCS", {"start": v(-15, 120) * mm, "mid": v(0, 135) * mm, "end": v(15, 120) * mm});
            skLineSegment(sketch, "E88.MirrorCS", {"start": v(80, 0) * mm, "end": v(-80, 0) * mm, "construction": true});
            skPoint(sketch, "E89.MirrorP", {"position": v(0, -90) * mm});
            skArc(sketch, "E90.MirrorCS", {"start": v(15, -120) * mm, "mid": v(0, -135) * mm, "end": v(-15, -120) * mm});
            skCircle(sketch, "E91.MirrorC", {"center": v(0, -120) * mm, "radius": 6 * mm});
            skLineSegment(sketch, "E92.MirrorCS", {"start": v(-15, -108) * mm, "end": v(-15, -120) * mm});
            skLineSegment(sketch, "E93.MirrorCS", {"start": v(-33, -90) * mm, "end": v(-15, -108) * mm});
            skLineSegment(sketch, "E94.MirrorCS", {"start": v(33, -90) * mm, "end": v(15, -108) * mm});
            skLineSegment(sketch, "E95.MirrorCS", {"start": v(15, -108) * mm, "end": v(15, -120) * mm});
            skArc(sketch, "E96.MirrorCS", {"start": v(-15, -120) * mm, "mid": v(0, -135) * mm, "end": v(15, -120) * mm});
            skLineSegment(sketch, "E97.MirrorCS", {"start": v(0, -90) * mm, "end": v(0, -120) * mm, "construction": true});
            skSolve(sketch);
        }
        {
            var Q0;
            {var subQ0=sQuery(id+"F16.wireOp",EDGE,"E93.MirrorCS");Q0=makeQuery(id+"F16.imprint","IMPRINT",FACE,{"disambiguationData":[TD([[makeQuery(id+"F16.imprint","IMPRINT",EDGE,{"derivedFrom":subQ0}),1.0]])]});}
            var Q1;
            Q1=makeQuery(id+"F16.imprint","IMPRINT",FACE,{"disambiguationData":[TD([[makeQuery(id+"F16.imprint","IMPRINT",EDGE,{"derivedFrom":makeQuery(id+"F1.opExtrude","CAP_EDGE",EDGE,{"disambiguationData":[OSD([sQuery(id+"F0.wireOp",EDGE,"E1.left")])],"isStart":true})}),-1.0]])]});
            var Q2;
            Q2=makeQuery(id+"F16.imprint","IMPRINT",FACE,{"disambiguationData":[TD([[makeQuery(id+"F16.imprint","IMPRINT",EDGE,{"derivedFrom":sQuery(id+"F16.wireOp",EDGE,"E79")}),1.0]])]});
            var Q3;
            Q3=makeQuery(id+"F2.opExtrude","CAP_FACE",FACE,{"disambiguationData":[OSD([sQuery(id+"F0.wireOp",EDGE,"E12"),sQuery(id+"F0.wireOp",EDGE,"E13"),sQuery(id+"F0.wireOp",EDGE,"E14"),sQuery(id+"F0.wireOp",EDGE,"E15"),sQuery(id+"F0.wireOp",EDGE,"E17.filletArc"),sQuery(id+"F0.wireOp",EDGE,"E18.filletArc"),sQuery(id+"F0.wireOp",EDGE,"E19.filletArc"),sQuery(id+"F0.wireOp",EDGE,"E20.filletArc"),sQuery(id+"F0.wireOp",EDGE,"E25.0"),sQuery(id+"F0.wireOp",EDGE,"E25.1"),sQuery(id+"F0.wireOp",EDGE,"E25.2"),sQuery(id+"F0.wireOp",EDGE,"E25.3"),sQuery(id+"F0.wireOp",EDGE,"E25.4"),sQuery(id+"F0.wireOp",EDGE,"E25.5"),sQuery(id+"F0.wireOp",EDGE,"E25.6"),sQuery(id+"F0.wireOp",EDGE,"E25.7")])],"isStart":false});
            extrude(context, id + "F17", {"entities" : qUnion([Q0, Q1, Q2]), "endBound" : BoundingType.UP_TO_SURFACE, "endBoundEntityFace" : qUnion([Q3]), "depth" : 10 * mm});
        }
    });
